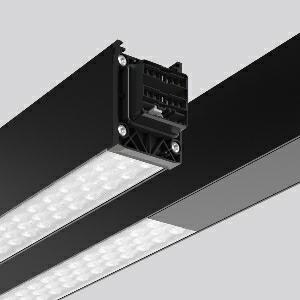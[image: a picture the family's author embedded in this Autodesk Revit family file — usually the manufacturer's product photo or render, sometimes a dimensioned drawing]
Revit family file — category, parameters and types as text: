
# Revit family: linedo_4_5m_30_11001100_954530_833_500_504_9d6d
name_source: partatom
category: Lighting Fixtures
units: mm (PartAtom-declared; Revit-internal decimal feet)

## family parameters
Cut with Voids When Loaded = No
Host = Face
Light Source = No
Part Type = Normal
Room Calculation Point = No
Round Connector Dimension = Use Diameter
Shared = No

## types (1)
- LINEDO_4,5m_30_11001100 (1 x LED Modul 830, 4950 lm, 3000)
    Apparent Load = 137 VA
    CIE Flux Codes = 89 97 99 100 100
    Color Rendering = 80
    Color Temperature = 3000
    Default Elevation = 1800 mm
    Description = LINEDO, 137 W, 19800 lm, 830, black, on/off
Continuous line luminaire, L 4547 B 58 H 76
    Height = 76 mm
    Lamp = 1 x LED Modul 830
    Lamp Light Flux = 4950 lm
    Lamp count = 1
    Length = 4547 mm
    Lifetime = 50000 h
    Luminous efficacy = 145 lm/W
    Manufacturer = RZB
    ModVariant = No
    Model = 954530.833.500.504
    Mounting Place = Ceiling
    Mounting Type = Surface mounted, Pendant
    Number of Poles = 1
    OnlyDefault = Yes
    Power Factor = 1
    Product Name = LINEDO_4,5m_30_11001100
    Product group = Surface mounted continuous line luminaire system
    ProductGroupID = 310
    Protection Class = Protection class I
    Protection Degree = IP 54
    RLX_Detail_Level = 1
    RLX_Emergency_Light_Flux = 0 lm
    RLX_Emergency_Type = 0
    RLX_Emergency_Type_DB = No
    RlxData = <blob elided: 56877 chars, md5=0d2af7b9>
    Socket = socket
    Standby Power = 0 W
    System Light Flux = 19800 lm
    System Power = 137 W
    Type Comments = Product without accessories
    Type Image = 954530.853.476.504.jpg
    URL = http://relux.com
    VarID = ---
    Voltage = 230 V
    Voltage Range = 220-240 V
    Weight = 0.00 kg
    Width = 58 mm

## geometry (parser evidence)
native form markers: Blend x4, Sweep x20
no freeform markers — native parametric forms only
